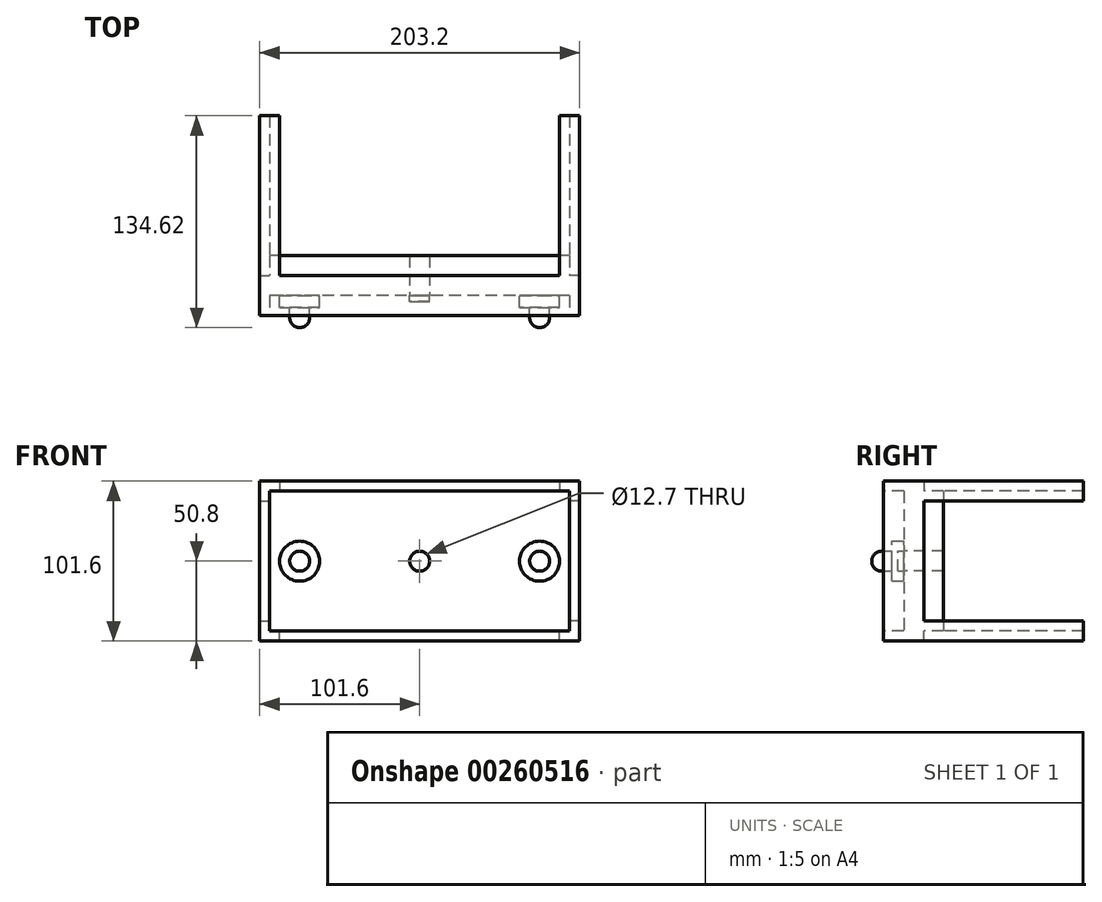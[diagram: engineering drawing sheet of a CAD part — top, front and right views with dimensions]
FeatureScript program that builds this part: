
annotation { "Feature Type Name" : "Feature", "Feature Type Description" : "" }
export const myFeature = defineFeature(function(context is Context, id is Id, definition is map)
    precondition{}
    {
        {
            var Q0;
            Q0=qCreatedBy(makeId("Front.planeOp"),FACE);
            var sketch = newSketch(context, id + "F0", { "sketchPlane" : qUnion([Q0])});
            skLineSegment(sketch, "E0.bottom", {"start": v(101.6, -50.8) * mm, "end": v(-101.6, -50.8) * mm});
            skLineSegment(sketch, "E0.top", {"start": v(101.6, 50.8) * mm, "end": v(-101.6, 50.8) * mm});
            skLineSegment(sketch, "E0.left", {"start": v(101.6, -50.8) * mm, "end": v(101.6, 50.8) * mm});
            skLineSegment(sketch, "E0.right", {"start": v(-101.6, -50.8) * mm, "end": v(-101.6, 50.8) * mm});
            skPoint(sketch, "E0.middle", {"position": v(0, 0) * mm});
            skLineSegment(sketch, "E1.bottom", {"start": v(95.25, 44.45) * mm, "end": v(-95.25, 44.45) * mm});
            skLineSegment(sketch, "E1.top", {"start": v(95.25, -44.45) * mm, "end": v(-95.25, -44.45) * mm});
            skLineSegment(sketch, "E1.left", {"start": v(95.25, 44.45) * mm, "end": v(95.25, -44.45) * mm});
            skLineSegment(sketch, "E1.right", {"start": v(-95.25, 44.45) * mm, "end": v(-95.25, -44.45) * mm});
            skCircle(sketch, "E2", {"center": v(0, 0) * mm, "radius": 6.35 * mm});
            skSolve(sketch);
        }
        {
            var Q0;
            Q0=makeQuery(id+"F0.imprint","IMPRINT",FACE,{"disambiguationData":[TD([[makeQuery(id+"F0.imprint","IMPRINT",EDGE,{"derivedFrom":sQuery(id+"F0.wireOp",EDGE,"E0.bottom")}),-1.0]])]});
            extrude(context, id + "F1", {"entities" : qUnion([Q0]), "oppositeDirection" : true, "depth" : 12.7 * mm});
        }
        {
            var Q0;
            Q0=makeQuery(id+"F1.opExtrude","CAP_FACE",FACE,{"disambiguationData":[OSD([sQuery(id+"F0.wireOp",EDGE,"E0.bottom"),sQuery(id+"F0.wireOp",EDGE,"E0.top"),sQuery(id+"F0.wireOp",EDGE,"E0.left"),sQuery(id+"F0.wireOp",EDGE,"E0.right")])],"isStart":false});
            var sketch = newSketch(context, id + "F2", { "sketchPlane" : qUnion([Q0])});
            skLineSegment(sketch, "E3.bottom", {"start": v(101.6, -50.8) * mm, "end": v(88.9, -50.8) * mm});
            skLineSegment(sketch, "E3.top", {"start": v(101.6, -38.1) * mm, "end": v(88.9, -38.1) * mm});
            skLineSegment(sketch, "E3.left", {"start": v(101.6, -50.8) * mm, "end": v(101.6, -38.1) * mm});
            skLineSegment(sketch, "E3.right", {"start": v(88.9, -50.8) * mm, "end": v(88.9, -38.1) * mm});
            skLineSegment(sketch, "E4.bottom", {"start": v(-101.6, -50.8) * mm, "end": v(-88.9, -50.8) * mm});
            skLineSegment(sketch, "E4.top", {"start": v(-101.6, -38.1) * mm, "end": v(-88.9, -38.1) * mm});
            skLineSegment(sketch, "E4.left", {"start": v(-101.6, -50.8) * mm, "end": v(-101.6, -38.1) * mm});
            skLineSegment(sketch, "E4.right", {"start": v(-88.9, -50.8) * mm, "end": v(-88.9, -38.1) * mm});
            skLineSegment(sketch, "E5.bottom", {"start": v(101.6, 50.8) * mm, "end": v(88.9, 50.8) * mm});
            skLineSegment(sketch, "E5.top", {"start": v(101.6, 38.1) * mm, "end": v(88.9, 38.1) * mm});
            skLineSegment(sketch, "E5.left", {"start": v(101.6, 50.8) * mm, "end": v(101.6, 38.1) * mm});
            skLineSegment(sketch, "E5.right", {"start": v(88.9, 50.8) * mm, "end": v(88.9, 38.1) * mm});
            skLineSegment(sketch, "E6.bottom", {"start": v(-101.6, 50.8) * mm, "end": v(-88.9, 50.8) * mm});
            skLineSegment(sketch, "E6.top", {"start": v(-101.6, 38.1) * mm, "end": v(-88.9, 38.1) * mm});
            skLineSegment(sketch, "E6.left", {"start": v(-101.6, 50.8) * mm, "end": v(-101.6, 38.1) * mm});
            skLineSegment(sketch, "E6.right", {"start": v(-88.9, 50.8) * mm, "end": v(-88.9, 38.1) * mm});
            skSolve(sketch);
        }
        {
            var Q0;
            Q0=makeQuery(id+"F2.imprint","IMPRINT",FACE,{"disambiguationData":[TD([[makeQuery(id+"F2.imprint","IMPRINT",EDGE,{"derivedFrom":sQuery(id+"F2.wireOp",EDGE,"E3.bottom")}),1.0]])]});
            var Q1;
            Q1=makeQuery(id+"F2.imprint","IMPRINT",FACE,{"disambiguationData":[TD([[makeQuery(id+"F2.imprint","IMPRINT",EDGE,{"derivedFrom":sQuery(id+"F2.wireOp",EDGE,"E4.bottom")}),1.0]])]});
            var Q2;
            Q2=makeQuery(id+"F2.imprint","IMPRINT",FACE,{"disambiguationData":[TD([[makeQuery(id+"F2.imprint","IMPRINT",EDGE,{"derivedFrom":sQuery(id+"F2.wireOp",EDGE,"E6.bottom")}),-1.0]])]});
            var Q3;
            Q3=makeQuery(id+"F2.imprint","IMPRINT",FACE,{"disambiguationData":[TD([[makeQuery(id+"F2.imprint","IMPRINT",EDGE,{"derivedFrom":sQuery(id+"F2.wireOp",EDGE,"E5.bottom")}),-1.0]])]});
            extrude(context, id + "F3", {"entities" : qUnion([Q0, Q1, Q2, Q3]), "operationType" : NewBodyOperationType.ADD, "depth" : 101.6 * mm});
        }
        {
            var Q0;
            Q0=makeQuery(id+"F0.imprint","IMPRINT",FACE,{"disambiguationData":[TD([[makeQuery(id+"F0.imprint","IMPRINT",EDGE,{"derivedFrom":sQuery(id+"F0.wireOp",EDGE,"E0.bottom")}),-1.0]])]});
            extrude(context, id + "F4", {"entities" : qUnion([Q0]), "operationType" : NewBodyOperationType.ADD, "depth" : 12.7 * mm});
        }
        {
            var Q0;
            Q0=makeQuery(id+"F0.imprint","IMPRINT",FACE,{"disambiguationData":[TD([[makeQuery(id+"F0.imprint","IMPRINT",EDGE,{"derivedFrom":sQuery(id+"F0.wireOp",EDGE,"E1.bottom")}),1.0]])]});
            extrude(context, id + "F5", {"entities" : qUnion([Q0]), "operationType" : NewBodyOperationType.ADD, "oppositeDirection" : true, "depth" : 25.4 * mm});
        }
        {
            var Q0;
            Q0=makeQuery(id+"F0.imprint","IMPRINT",FACE,{"disambiguationData":[TD([[makeQuery(id+"F0.imprint","IMPRINT",EDGE,{"derivedFrom":sQuery(id+"F0.wireOp",EDGE,"E2")}),1.0]])]});
            extrude(context, id + "F6", {"entities" : qUnion([Q0]), "depth" : 3.8 * mm});
        }
        {
            var Q0;
            Q0=qCreatedBy(makeId("Front.planeOp"),FACE);
            var sketch = newSketch(context, id + "F7", { "sketchPlane" : qUnion([Q0])});
            skLineSegment(sketch, "E7", {"start": v(0, 0) * mm, "end": v(-76.2, 0) * mm});
            skLineSegment(sketch, "E8", {"start": v(0, 0) * mm, "end": v(76.2, 0) * mm});
            skCircle(sketch, "E9", {"center": v(-76.2, 0) * mm, "radius": 12.7 * mm});
            skCircle(sketch, "E10", {"center": v(-76.2, 0) * mm, "radius": 6.35 * mm});
            skCircle(sketch, "E11", {"center": v(76.2, 0) * mm, "radius": 12.7 * mm});
            skCircle(sketch, "E12", {"center": v(76.2, 0) * mm, "radius": 6.35 * mm});
            skSolve(sketch);
        }
        {
            var Q0;
            Q0=makeQuery(id+"F7.imprint","IMPRINT",FACE,{"disambiguationData":[TD([[makeQuery(id+"F7.imprint","IMPRINT",EDGE,{"derivedFrom":sQuery(id+"F7.wireOp",EDGE,"E9")}),1.0]])]});
            var Q1;
            Q1=makeQuery(id+"F7.imprint","IMPRINT",FACE,{"disambiguationData":[TD([[makeQuery(id+"F7.imprint","IMPRINT",EDGE,{"derivedFrom":sQuery(id+"F7.wireOp",EDGE,"E11")}),1.0]])]});
            extrude(context, id + "F8", {"entities" : qUnion([Q0, Q1]), "operationType" : NewBodyOperationType.ADD, "depth" : 7.62 * mm});
        }
        {
            var Q0;
            Q0=makeQuery(id+"F8.boolean.opBoolean","SPLIT",FACE,{"disambiguationData":[TD([makeQuery(id+"F8.opExtrude","SWEPT_FACE",FACE,{"disambiguationData":[OSD([sQuery(id+"F7.wireOp",EDGE,"E10")])]})])],"derivedFrom":makeQuery(id+"F5.opExtrude","CAP_FACE",FACE,{"disambiguationData":[OSD([sQuery(id+"F0.wireOp",EDGE,"E1.bottom"),sQuery(id+"F0.wireOp",EDGE,"E1.top"),sQuery(id+"F0.wireOp",EDGE,"E1.left"),sQuery(id+"F0.wireOp",EDGE,"E1.right"),sQuery(id+"F0.wireOp",EDGE,"E2")])],"isStart":true})});
            var Q1;
            Q1=makeQuery(id+"F8.boolean.opBoolean","SPLIT",FACE,{"disambiguationData":[TD([makeQuery(id+"F8.opExtrude","SWEPT_FACE",FACE,{"disambiguationData":[OSD([sQuery(id+"F7.wireOp",EDGE,"E12")])]})])],"derivedFrom":makeQuery(id+"F5.opExtrude","CAP_FACE",FACE,{"disambiguationData":[OSD([sQuery(id+"F0.wireOp",EDGE,"E1.bottom"),sQuery(id+"F0.wireOp",EDGE,"E1.top"),sQuery(id+"F0.wireOp",EDGE,"E1.left"),sQuery(id+"F0.wireOp",EDGE,"E1.right"),sQuery(id+"F0.wireOp",EDGE,"E2")])],"isStart":true})});
            extrude(context, id + "F9", {"entities" : qUnion([Q0, Q1]), "operationType" : NewBodyOperationType.ADD, "depth" : 20.32 * mm});
        }
        {
            var Q0;
            Q0=makeQuery(id+"F9.opExtrude","CAP_EDGE",EDGE,{"disambiguationData":[OSD([sQuery(id+"F7.wireOp",EDGE,"E10")])],"isStart":false});
            var Q1;
            Q1=makeQuery(id+"F9.opExtrude","CAP_EDGE",EDGE,{"disambiguationData":[OSD([sQuery(id+"F7.wireOp",EDGE,"E12")])],"isStart":false});
            fillet(context, id + "F10", {"entities" : qUnion([Q0, Q1]), "radius" : 6.35 * mm, "tangentPropagation" : true, "allowEdgeOverflow" : false});
        }
    });
